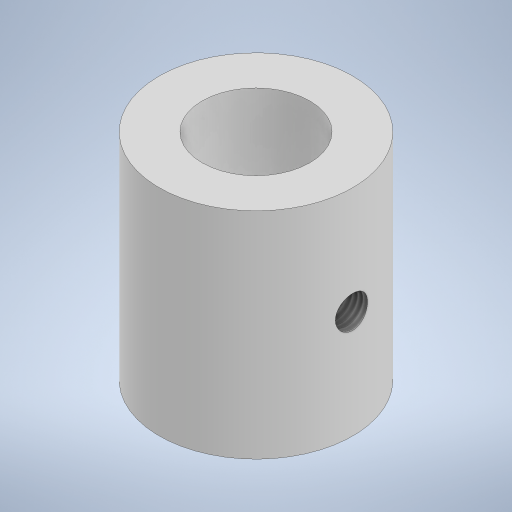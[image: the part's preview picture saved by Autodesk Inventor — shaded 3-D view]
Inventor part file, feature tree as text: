
AUTODESK INVENTOR PART (.ipt)
format: ipt  version: 2023 (Build 270158000, 158)  size: 220,672 bytes
history: native  units: mm
features: extrude x2, sketch x2, other x1, thread x1
ambient origin geometry x8: Origin, YZ Plane, XZ Plane, XY Plane, X Axis, Y Axis, Z Axis, Center Point
bodies: Body1 (feature_tree)
feature tree (6):
  other  "Твердое тело1"
  extrude  "Выдавливание1"  Depth=10.0mm
  extrude  "Выдавливание2"  Depth=18.0mm
  thread  "Резьба1"
  sketch  "Эскиз1"
  sketch  "Эскиз2"
